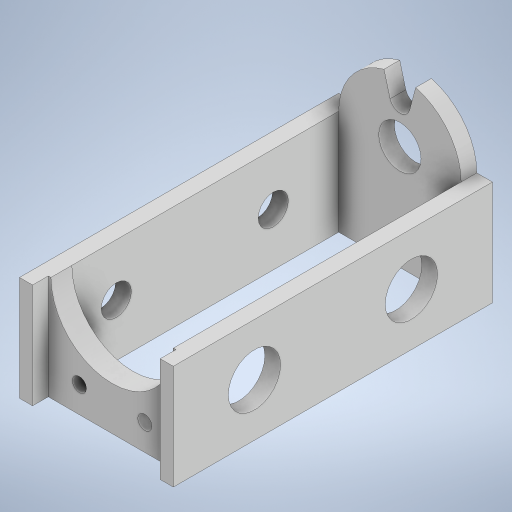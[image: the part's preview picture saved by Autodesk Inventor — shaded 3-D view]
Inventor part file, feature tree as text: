
AUTODESK INVENTOR PART (.ipt)
format: ipt  version: 2023 (Build 270158000, 158)  size: 318,464 bytes
history: native  units: mm
features: extrude x8, sketch x8
ambient origin geometry x8: Origin, YZ Plane, XZ Plane, XY Plane, X Axis, Y Axis, Z Axis, Center Point
bodies: Solid1 (feature_tree)
feature tree (16):
  extrude  "Extrusion1"  Depth=3.0mm TaperAngle=0.0deg
  extrude  "Extrusion2"  Depth=1.5mm
  extrude  "Extrusion3"  Depth=3.0mm TaperAngle=0.0deg
  extrude  "Extrusion4"  Depth=4.0mm
  extrude  "Extrusion5"  Depth=15.0mm
  extrude  "Extrusion7"  Depth=3.0mm TaperAngle=0.0deg
  extrude  "Extrusion6"  Depth=5.7625mm
  extrude  "Extrusion8"  Depth=10.0mm TaperAngle=0.0deg
  sketch  "Sketch1"  dims[d0=23.4mm d3=8.1mm d4=20.0mm d6=3.0mm d7=0.0mm]
  sketch  "Sketch2"  dims[d8=30.0deg d9=1.5mm]
  sketch  "Sketch3"  dims[d10=55.0mm d11=3.0mm d12=0.0mm]
  sketch  "Sketch4"  dims[d13=4.0mm d14=0.0mm d15=12.5mm]
  sketch  "Sketch5"  dims[d16=2.7mm d17=15.0mm]
  sketch  "Sketch6"  dims[d18=2.5mm d19=0.0mm d20=3.0mm d21=0.0mm]
  sketch  "Sketch7"  dims[d22=30.0mm d23=5.7625mm]
  sketch  "Sketch8"  dims[d24=10.0mm d25=10.0mm d26=0.0mm d27=2.5mm d28=3.0mm d29=0.0mm d30=10.0mm d31=3.0mm d32=0.0mm]
